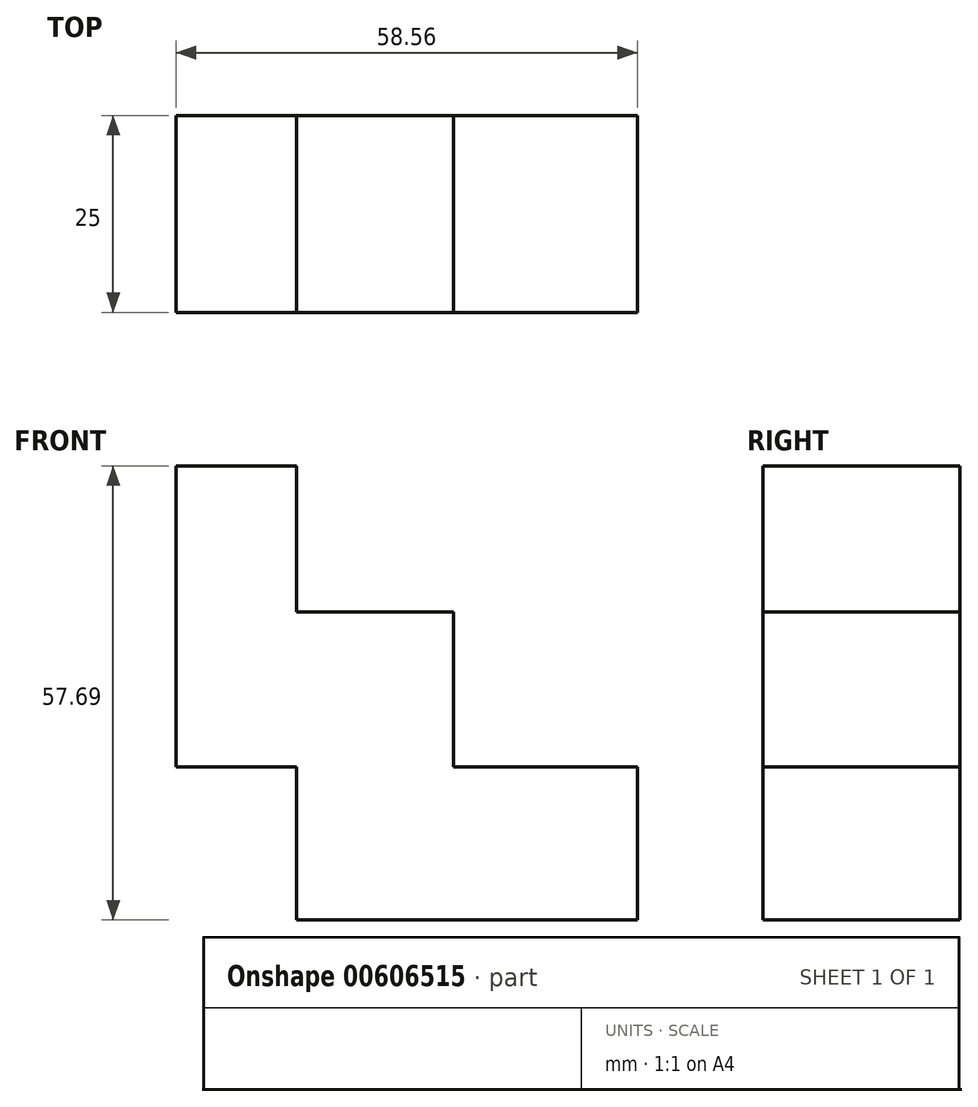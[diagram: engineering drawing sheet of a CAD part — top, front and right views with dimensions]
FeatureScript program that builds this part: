
annotation { "Feature Type Name" : "Feature", "Feature Type Description" : "" }
export const myFeature = defineFeature(function(context is Context, id is Id, definition is map)
    precondition{}
    {
        {
            var Q0;
            Q0=qCreatedBy(makeId("Front.planeOp"),FACE);
            var sketch = newSketch(context, id + "F0", { "sketchPlane" : qUnion([Q0])});
            skLineSegment(sketch, "E0", {"start": v(-62.25, 36) * mm, "end": v(-62.25, -2.23) * mm});
            skLineSegment(sketch, "E1", {"start": v(-62.25, -2.23) * mm, "end": v(-47, -2.23) * mm});
            skLineSegment(sketch, "E2", {"start": v(-47, -2.23) * mm, "end": v(-47, -21.65) * mm});
            skLineSegment(sketch, "E3", {"start": v(-47, -21.65) * mm, "end": v(-21.26, -21.65) * mm});
            skLineSegment(sketch, "E4", {"start": v(-21.26, -21.65) * mm, "end": v(-3.7, -21.65) * mm});
            skLineSegment(sketch, "E5", {"start": v(-3.7, -21.65) * mm, "end": v(-3.7, -2.23) * mm});
            skLineSegment(sketch, "E6", {"start": v(-3.7, -2.23) * mm, "end": v(-27, -2.23) * mm});
            skLineSegment(sketch, "E7", {"start": v(-27, -2.23) * mm, "end": v(-27, 17.47) * mm});
            skLineSegment(sketch, "E8", {"start": v(-27, 17.47) * mm, "end": v(-47, 17.47) * mm});
            skLineSegment(sketch, "E9", {"start": v(-47, 17.47) * mm, "end": v(-47, 36.04) * mm});
            skLineSegment(sketch, "E10", {"start": v(-47, 36.04) * mm, "end": v(-62.25, 36) * mm});
            skSolve(sketch);
        }
        {
            var Q0;
            Q0=makeQuery(id+"F0.imprint","IMPRINT",FACE,{"disambiguationData":[TD([[makeQuery(id+"F0.imprint","IMPRINT",EDGE,{"derivedFrom":sQuery(id+"F0.wireOp",EDGE,"E0")}),1.0]])]});
            extrude(context, id + "F1", {"entities" : qUnion([Q0]), "depth" : 25 * mm, "offsetDistance" : 25 * mm});
        }
    });
